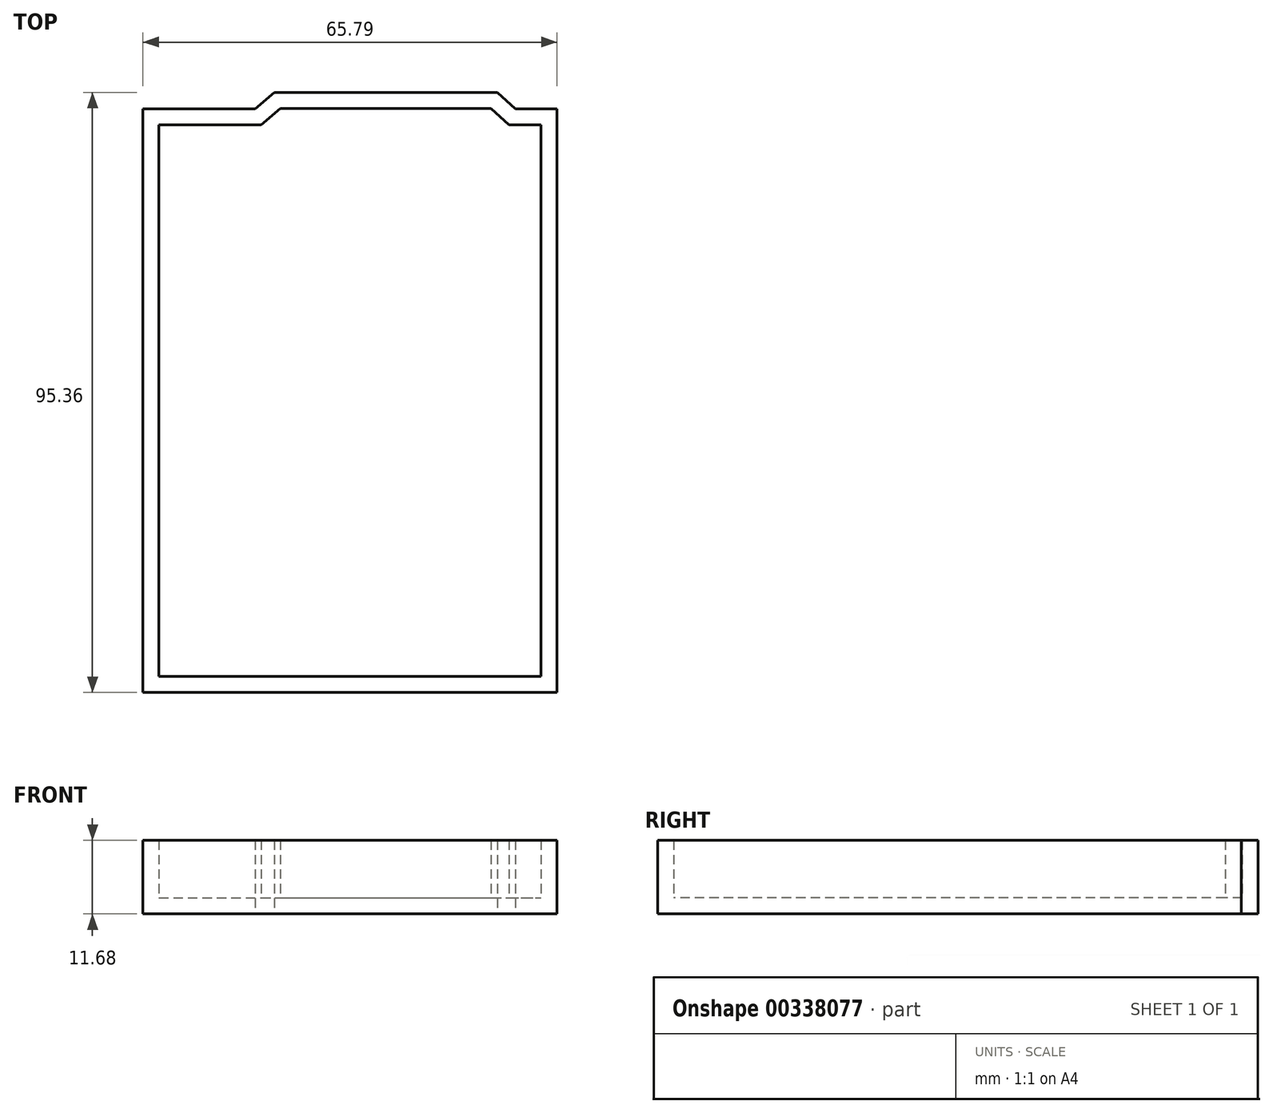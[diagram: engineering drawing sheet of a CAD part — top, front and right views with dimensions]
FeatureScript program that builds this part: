
annotation { "Feature Type Name" : "Feature", "Feature Type Description" : "" }
export const myFeature = defineFeature(function(context is Context, id is Id, definition is map)
    precondition{}
    {
        {
            var Q0;
            Q0=qCreatedBy(makeId("Top.planeOp"),FACE);
            var sketch = newSketch(context, id + "F0", { "sketchPlane" : qUnion([Q0])});
            skLineSegment(sketch, "E0.bottom", {"start": v(-32.42, 38.1) * mm, "end": v(33.37, 38.1) * mm});
            skLineSegment(sketch, "E0.top", {"start": v(-32.42, -54.6) * mm, "end": v(33.37, -54.6) * mm});
            skLineSegment(sketch, "E0.left", {"start": v(-32.42, 38.1) * mm, "end": v(-32.42, -54.6) * mm});
            skLineSegment(sketch, "E0.right", {"start": v(33.37, 38.1) * mm, "end": v(33.37, -54.6) * mm});
            skLineSegment(sketch, "E1", {"start": v(-14.6, 38.1) * mm, "end": v(-11.57, 40.76) * mm});
            skLineSegment(sketch, "E2", {"start": v(-11.57, 40.76) * mm, "end": v(23.89, 40.76) * mm});
            skLineSegment(sketch, "E3", {"start": v(23.89, 40.76) * mm, "end": v(26.73, 38.1) * mm});
            skSolve(sketch);
        }
        {
            var Q0;
            Q0 = qSketchRegion(id + "F0", true);
            extrude(context, id + "F1", {"entities" : qUnion([Q0]), "depth" : 11.68 * mm});
        }
        {
            var Q0;
            Q0=makeQuery(id+"F1.opExtrude","CAP_FACE",FACE,{"disambiguationData":[OSD([sQuery(id+"F0.wireOp",EDGE,"E0.bottom"),sQuery(id+"F0.wireOp",EDGE,"E0.top"),sQuery(id+"F0.wireOp",EDGE,"E0.left"),sQuery(id+"F0.wireOp",EDGE,"E0.right"),sQuery(id+"F0.wireOp",EDGE,"E1"),sQuery(id+"F0.wireOp",EDGE,"E2"),sQuery(id+"F0.wireOp",EDGE,"E3")])],"isStart":false});
            shell(context, id + "F2", {"entities" : qUnion([Q0]), "thickness" : 2.54 * mm});
        }
    });
